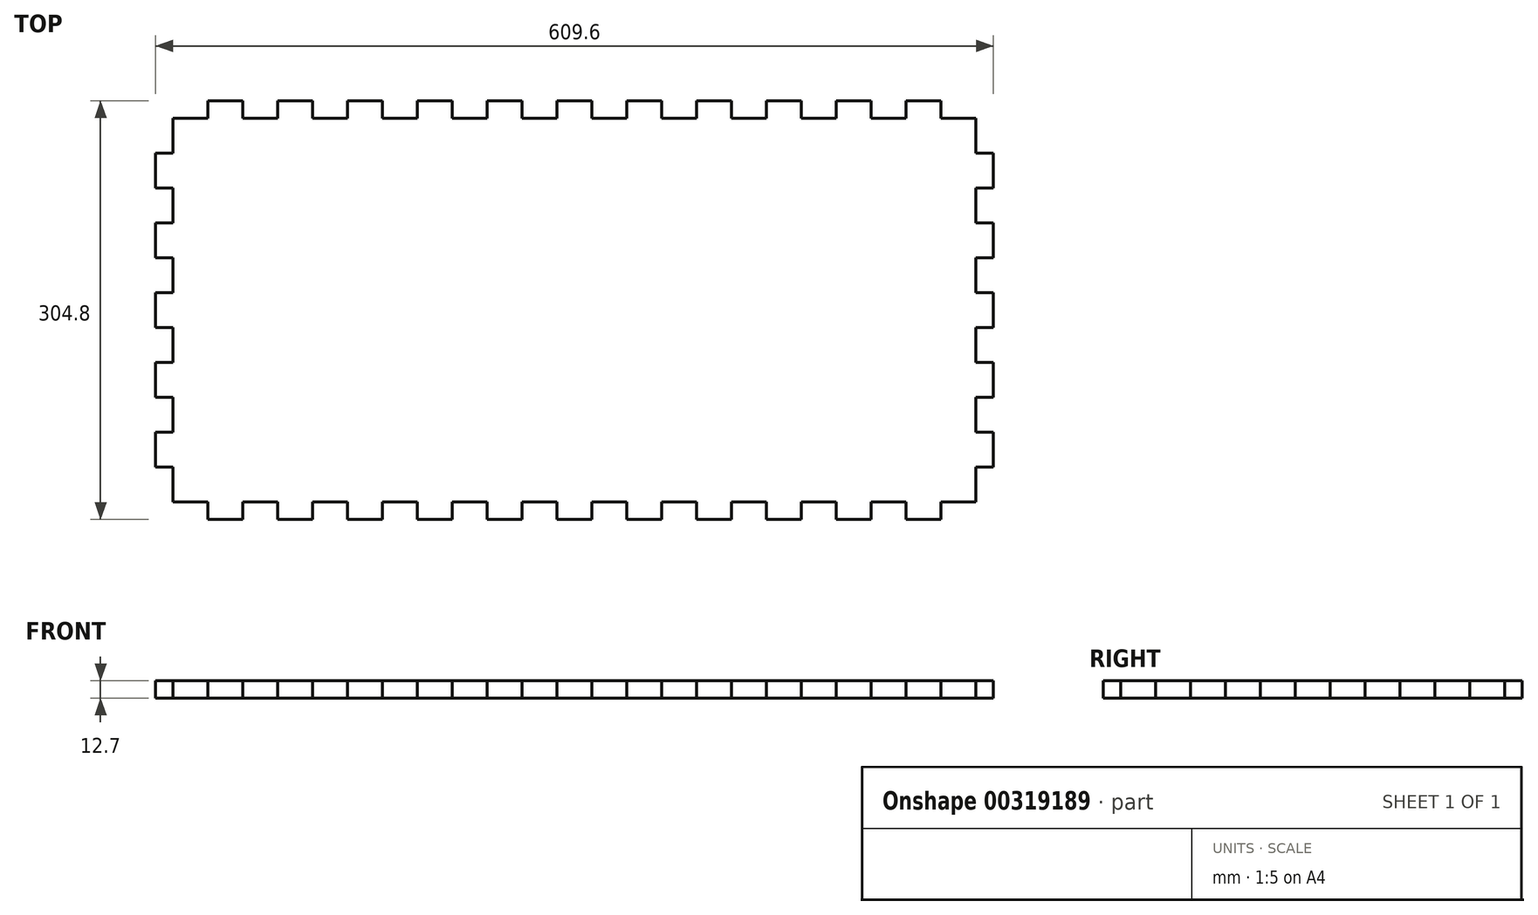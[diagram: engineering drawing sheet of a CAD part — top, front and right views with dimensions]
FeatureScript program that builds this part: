
annotation { "Feature Type Name" : "Feature", "Feature Type Description" : "" }
export const myFeature = defineFeature(function(context is Context, id is Id, definition is map)
    precondition{}
    {
        {
            var Q0;
            Q0=qCreatedBy(makeId("Top.planeOp"),FACE);
            var sketch = newSketch(context, id + "F0", { "sketchPlane" : qUnion([Q0])});
            skLineSegment(sketch, "E0.bottom", {"start": v(304.8, 152.4) * mm, "end": v(-304.8, 152.4) * mm});
            skLineSegment(sketch, "E0.top", {"start": v(304.8, -152.4) * mm, "end": v(-304.8, -152.4) * mm});
            skLineSegment(sketch, "E0.left", {"start": v(304.8, 152.4) * mm, "end": v(304.8, -152.4) * mm});
            skLineSegment(sketch, "E0.right", {"start": v(-304.8, 152.4) * mm, "end": v(-304.8, -152.4) * mm});
            skPoint(sketch, "E0.middle", {"position": v(0, 0) * mm});
            skLineSegment(sketch, "E1.bottom", {"start": v(-292.1, 152.4) * mm, "end": v(-266.7, 152.4) * mm});
            skLineSegment(sketch, "E1.top", {"start": v(-292.1, 139.7) * mm, "end": v(-266.7, 139.7) * mm});
            skLineSegment(sketch, "E1.left", {"start": v(-292.1, 152.4) * mm, "end": v(-292.1, 139.7) * mm});
            skLineSegment(sketch, "E1.right", {"start": v(-266.7, 152.4) * mm, "end": v(-266.7, 139.7) * mm});
            skLineSegment(sketch, "E2.1.0.0", {"start": v(-241.3, 152.4) * mm, "end": v(-241.3, 139.7) * mm});
            skLineSegment(sketch, "E2.1.0.1", {"start": v(-215.9, 152.4) * mm, "end": v(-215.9, 139.7) * mm});
            skLineSegment(sketch, "E2.1.0.2", {"start": v(-241.3, 139.7) * mm, "end": v(-215.9, 139.7) * mm});
            skLineSegment(sketch, "E2.1.0.3", {"start": v(-241.3, 152.4) * mm, "end": v(-215.9, 152.4) * mm});
            skLineSegment(sketch, "E2.2.0.0", {"start": v(-190.5, 152.4) * mm, "end": v(-190.5, 139.7) * mm});
            skLineSegment(sketch, "E2.2.0.1", {"start": v(-165.1, 152.4) * mm, "end": v(-165.1, 139.7) * mm});
            skLineSegment(sketch, "E2.2.0.2", {"start": v(-190.5, 139.7) * mm, "end": v(-165.1, 139.7) * mm});
            skLineSegment(sketch, "E2.2.0.3", {"start": v(-190.5, 152.4) * mm, "end": v(-165.1, 152.4) * mm});
            skLineSegment(sketch, "E2.3.0.0", {"start": v(-139.7, 152.4) * mm, "end": v(-139.7, 139.7) * mm});
            skLineSegment(sketch, "E2.3.0.1", {"start": v(-114.3, 152.4) * mm, "end": v(-114.3, 139.7) * mm});
            skLineSegment(sketch, "E2.3.0.2", {"start": v(-139.7, 139.7) * mm, "end": v(-114.3, 139.7) * mm});
            skLineSegment(sketch, "E2.3.0.3", {"start": v(-139.7, 152.4) * mm, "end": v(-114.3, 152.4) * mm});
            skLineSegment(sketch, "E2.4.0.0", {"start": v(-88.9, 152.4) * mm, "end": v(-88.9, 139.7) * mm});
            skLineSegment(sketch, "E2.4.0.1", {"start": v(-63.5, 152.4) * mm, "end": v(-63.5, 139.7) * mm});
            skLineSegment(sketch, "E2.4.0.2", {"start": v(-88.9, 139.7) * mm, "end": v(-63.5, 139.7) * mm});
            skLineSegment(sketch, "E2.4.0.3", {"start": v(-88.9, 152.4) * mm, "end": v(-63.5, 152.4) * mm});
            skLineSegment(sketch, "E2.5.0.0", {"start": v(-38.1, 152.4) * mm, "end": v(-38.1, 139.7) * mm});
            skLineSegment(sketch, "E2.5.0.1", {"start": v(-12.7, 152.4) * mm, "end": v(-12.7, 139.7) * mm});
            skLineSegment(sketch, "E2.5.0.2", {"start": v(-38.1, 139.7) * mm, "end": v(-12.7, 139.7) * mm});
            skLineSegment(sketch, "E2.5.0.3", {"start": v(-38.1, 152.4) * mm, "end": v(-12.7, 152.4) * mm});
            skLineSegment(sketch, "E2.6.0.0", {"start": v(12.7, 152.4) * mm, "end": v(12.7, 139.7) * mm});
            skLineSegment(sketch, "E2.6.0.1", {"start": v(38.1, 152.4) * mm, "end": v(38.1, 139.7) * mm});
            skLineSegment(sketch, "E2.6.0.2", {"start": v(12.7, 139.7) * mm, "end": v(38.1, 139.7) * mm});
            skLineSegment(sketch, "E2.6.0.3", {"start": v(12.7, 152.4) * mm, "end": v(38.1, 152.4) * mm});
            skLineSegment(sketch, "E2.7.0.0", {"start": v(63.5, 152.4) * mm, "end": v(63.5, 139.7) * mm});
            skLineSegment(sketch, "E2.7.0.1", {"start": v(88.9, 152.4) * mm, "end": v(88.9, 139.7) * mm});
            skLineSegment(sketch, "E2.7.0.2", {"start": v(63.5, 139.7) * mm, "end": v(88.9, 139.7) * mm});
            skLineSegment(sketch, "E2.7.0.3", {"start": v(63.5, 152.4) * mm, "end": v(88.9, 152.4) * mm});
            skLineSegment(sketch, "E2.8.0.0", {"start": v(114.3, 152.4) * mm, "end": v(114.3, 139.7) * mm});
            skLineSegment(sketch, "E2.8.0.1", {"start": v(139.7, 152.4) * mm, "end": v(139.7, 139.7) * mm});
            skLineSegment(sketch, "E2.8.0.2", {"start": v(114.3, 139.7) * mm, "end": v(139.7, 139.7) * mm});
            skLineSegment(sketch, "E2.8.0.3", {"start": v(114.3, 152.4) * mm, "end": v(139.7, 152.4) * mm});
            skLineSegment(sketch, "E2.9.0.0", {"start": v(165.1, 152.4) * mm, "end": v(165.1, 139.7) * mm});
            skLineSegment(sketch, "E2.9.0.1", {"start": v(190.5, 152.4) * mm, "end": v(190.5, 139.7) * mm});
            skLineSegment(sketch, "E2.9.0.2", {"start": v(165.1, 139.7) * mm, "end": v(190.5, 139.7) * mm});
            skLineSegment(sketch, "E2.9.0.3", {"start": v(165.1, 152.4) * mm, "end": v(190.5, 152.4) * mm});
            skLineSegment(sketch, "E2.10.0.0", {"start": v(215.9, 152.4) * mm, "end": v(215.9, 139.7) * mm});
            skLineSegment(sketch, "E2.10.0.1", {"start": v(241.3, 152.4) * mm, "end": v(241.3, 139.7) * mm});
            skLineSegment(sketch, "E2.10.0.2", {"start": v(215.9, 139.7) * mm, "end": v(241.3, 139.7) * mm});
            skLineSegment(sketch, "E2.10.0.3", {"start": v(215.9, 152.4) * mm, "end": v(241.3, 152.4) * mm});
            skLineSegment(sketch, "E2.11.0.0", {"start": v(266.7, 152.4) * mm, "end": v(266.7, 139.7) * mm});
            skLineSegment(sketch, "E2.11.0.1", {"start": v(292.1, 152.4) * mm, "end": v(292.1, 139.7) * mm});
            skLineSegment(sketch, "E2.11.0.2", {"start": v(266.7, 139.7) * mm, "end": v(292.1, 139.7) * mm});
            skLineSegment(sketch, "E2.11.0.3", {"start": v(266.7, 152.4) * mm, "end": v(292.1, 152.4) * mm});
            skLineSegment(sketch, "E2.direction1", {"start": v(-292.1, 139.7) * mm, "end": v(-241.3, 139.7) * mm, "construction": true});
            skLineSegment(sketch, "E3.bottom", {"start": v(-292.1, -152.4) * mm, "end": v(-266.7, -152.4) * mm});
            skLineSegment(sketch, "E3.top", {"start": v(-292.1, -139.7) * mm, "end": v(-266.7, -139.7) * mm});
            skLineSegment(sketch, "E3.left", {"start": v(-292.1, -152.4) * mm, "end": v(-292.1, -139.7) * mm});
            skLineSegment(sketch, "E3.right", {"start": v(-266.7, -152.4) * mm, "end": v(-266.7, -139.7) * mm});
            skLineSegment(sketch, "E4.bottom", {"start": v(-304.8, -114.3) * mm, "end": v(-292.1, -114.3) * mm});
            skLineSegment(sketch, "E4.top", {"start": v(-304.8, -139.7) * mm, "end": v(-292.1, -139.7) * mm});
            skLineSegment(sketch, "E4.left", {"start": v(-304.8, -114.3) * mm, "end": v(-304.8, -139.7) * mm});
            skLineSegment(sketch, "E4.right", {"start": v(-292.1, -114.3) * mm, "end": v(-292.1, -139.7) * mm});
            skLineSegment(sketch, "E5.1.0.0", {"start": v(-241.3, -139.7) * mm, "end": v(-215.9, -139.7) * mm});
            skLineSegment(sketch, "E5.1.0.1", {"start": v(-215.9, -152.4) * mm, "end": v(-215.9, -139.7) * mm});
            skLineSegment(sketch, "E5.1.0.2", {"start": v(-241.3, -152.4) * mm, "end": v(-241.3, -139.7) * mm});
            skLineSegment(sketch, "E5.2.0.0", {"start": v(-190.5, -139.7) * mm, "end": v(-165.1, -139.7) * mm});
            skLineSegment(sketch, "E5.2.0.1", {"start": v(-165.1, -152.4) * mm, "end": v(-165.1, -139.7) * mm});
            skLineSegment(sketch, "E5.2.0.2", {"start": v(-190.5, -152.4) * mm, "end": v(-190.5, -139.7) * mm});
            skLineSegment(sketch, "E5.3.0.0", {"start": v(-139.7, -139.7) * mm, "end": v(-114.3, -139.7) * mm});
            skLineSegment(sketch, "E5.3.0.1", {"start": v(-114.3, -152.4) * mm, "end": v(-114.3, -139.7) * mm});
            skLineSegment(sketch, "E5.3.0.2", {"start": v(-139.7, -152.4) * mm, "end": v(-139.7, -139.7) * mm});
            skLineSegment(sketch, "E5.4.0.0", {"start": v(-88.9, -139.7) * mm, "end": v(-63.5, -139.7) * mm});
            skLineSegment(sketch, "E5.4.0.1", {"start": v(-63.5, -152.4) * mm, "end": v(-63.5, -139.7) * mm});
            skLineSegment(sketch, "E5.4.0.2", {"start": v(-88.9, -152.4) * mm, "end": v(-88.9, -139.7) * mm});
            skLineSegment(sketch, "E5.5.0.0", {"start": v(-38.1, -139.7) * mm, "end": v(-12.7, -139.7) * mm});
            skLineSegment(sketch, "E5.5.0.1", {"start": v(-12.7, -152.4) * mm, "end": v(-12.7, -139.7) * mm});
            skLineSegment(sketch, "E5.5.0.2", {"start": v(-38.1, -152.4) * mm, "end": v(-38.1, -139.7) * mm});
            skLineSegment(sketch, "E5.6.0.0", {"start": v(12.7, -139.7) * mm, "end": v(38.1, -139.7) * mm});
            skLineSegment(sketch, "E5.6.0.1", {"start": v(38.1, -152.4) * mm, "end": v(38.1, -139.7) * mm});
            skLineSegment(sketch, "E5.6.0.2", {"start": v(12.7, -152.4) * mm, "end": v(12.7, -139.7) * mm});
            skLineSegment(sketch, "E5.7.0.0", {"start": v(63.5, -139.7) * mm, "end": v(88.9, -139.7) * mm});
            skLineSegment(sketch, "E5.7.0.1", {"start": v(88.9, -152.4) * mm, "end": v(88.9, -139.7) * mm});
            skLineSegment(sketch, "E5.7.0.2", {"start": v(63.5, -152.4) * mm, "end": v(63.5, -139.7) * mm});
            skLineSegment(sketch, "E5.8.0.0", {"start": v(114.3, -139.7) * mm, "end": v(139.7, -139.7) * mm});
            skLineSegment(sketch, "E5.8.0.1", {"start": v(139.7, -152.4) * mm, "end": v(139.7, -139.7) * mm});
            skLineSegment(sketch, "E5.8.0.2", {"start": v(114.3, -152.4) * mm, "end": v(114.3, -139.7) * mm});
            skLineSegment(sketch, "E5.9.0.0", {"start": v(165.1, -139.7) * mm, "end": v(190.5, -139.7) * mm});
            skLineSegment(sketch, "E5.9.0.1", {"start": v(190.5, -152.4) * mm, "end": v(190.5, -139.7) * mm});
            skLineSegment(sketch, "E5.9.0.2", {"start": v(165.1, -152.4) * mm, "end": v(165.1, -139.7) * mm});
            skLineSegment(sketch, "E5.10.0.0", {"start": v(215.9, -139.7) * mm, "end": v(241.3, -139.7) * mm});
            skLineSegment(sketch, "E5.10.0.1", {"start": v(241.3, -152.4) * mm, "end": v(241.3, -139.7) * mm});
            skLineSegment(sketch, "E5.10.0.2", {"start": v(215.9, -152.4) * mm, "end": v(215.9, -139.7) * mm});
            skLineSegment(sketch, "E5.11.0.0", {"start": v(266.7, -139.7) * mm, "end": v(292.1, -139.7) * mm});
            skLineSegment(sketch, "E5.11.0.1", {"start": v(292.1, -152.4) * mm, "end": v(292.1, -139.7) * mm});
            skLineSegment(sketch, "E5.11.0.2", {"start": v(266.7, -152.4) * mm, "end": v(266.7, -139.7) * mm});
            skLineSegment(sketch, "E5.direction1", {"start": v(-292.1, -139.7) * mm, "end": v(-241.3, -139.7) * mm, "construction": true});
            skLineSegment(sketch, "E6.0.1.0", {"start": v(-304.8, -88.9) * mm, "end": v(-292.1, -88.9) * mm});
            skLineSegment(sketch, "E6.0.1.1", {"start": v(-292.1, -63.5) * mm, "end": v(-292.1, -88.9) * mm});
            skLineSegment(sketch, "E6.0.1.2", {"start": v(-304.8, -63.5) * mm, "end": v(-292.1, -63.5) * mm});
            skLineSegment(sketch, "E6.0.2.0", {"start": v(-304.8, -38.1) * mm, "end": v(-292.1, -38.1) * mm});
            skLineSegment(sketch, "E6.0.2.1", {"start": v(-292.1, -12.7) * mm, "end": v(-292.1, -38.1) * mm});
            skLineSegment(sketch, "E6.0.2.2", {"start": v(-304.8, -12.7) * mm, "end": v(-292.1, -12.7) * mm});
            skLineSegment(sketch, "E6.0.3.0", {"start": v(-304.8, 12.7) * mm, "end": v(-292.1, 12.7) * mm});
            skLineSegment(sketch, "E6.0.3.1", {"start": v(-292.1, 38.1) * mm, "end": v(-292.1, 12.7) * mm});
            skLineSegment(sketch, "E6.0.3.2", {"start": v(-304.8, 38.1) * mm, "end": v(-292.1, 38.1) * mm});
            skLineSegment(sketch, "E6.0.4.0", {"start": v(-304.8, 63.5) * mm, "end": v(-292.1, 63.5) * mm});
            skLineSegment(sketch, "E6.0.4.1", {"start": v(-292.1, 88.9) * mm, "end": v(-292.1, 63.5) * mm});
            skLineSegment(sketch, "E6.0.4.2", {"start": v(-304.8, 88.9) * mm, "end": v(-292.1, 88.9) * mm});
            skLineSegment(sketch, "E6.0.5.0", {"start": v(-304.8, 114.3) * mm, "end": v(-292.1, 114.3) * mm});
            skLineSegment(sketch, "E6.0.5.1", {"start": v(-292.1, 139.7) * mm, "end": v(-292.1, 114.3) * mm});
            skLineSegment(sketch, "E6.0.5.2", {"start": v(-304.8, 139.7) * mm, "end": v(-292.1, 139.7) * mm});
            skLineSegment(sketch, "E6.direction1", {"start": v(-304.8, -139.7) * mm, "end": v(-279.4, -139.7) * mm, "construction": true});
            skLineSegment(sketch, "E6.direction2", {"start": v(-304.8, -139.7) * mm, "end": v(-304.8, -88.9) * mm, "construction": true});
            skLineSegment(sketch, "E7.bottom", {"start": v(304.8, -139.7) * mm, "end": v(292.1, -139.7) * mm});
            skLineSegment(sketch, "E7.top", {"start": v(304.8, -114.3) * mm, "end": v(292.1, -114.3) * mm});
            skLineSegment(sketch, "E7.left", {"start": v(304.8, -139.7) * mm, "end": v(304.8, -114.3) * mm});
            skLineSegment(sketch, "E7.right", {"start": v(292.1, -139.7) * mm, "end": v(292.1, -114.3) * mm});
            skLineSegment(sketch, "E8.0.1.0", {"start": v(304.8, -88.9) * mm, "end": v(304.8, -63.5) * mm});
            skLineSegment(sketch, "E8.0.1.1", {"start": v(304.8, -63.5) * mm, "end": v(292.1, -63.5) * mm});
            skLineSegment(sketch, "E8.0.1.2", {"start": v(304.8, -88.9) * mm, "end": v(292.1, -88.9) * mm});
            skLineSegment(sketch, "E8.0.1.3", {"start": v(292.1, -88.9) * mm, "end": v(292.1, -63.5) * mm});
            skLineSegment(sketch, "E8.0.2.0", {"start": v(304.8, -38.1) * mm, "end": v(304.8, -12.7) * mm});
            skLineSegment(sketch, "E8.0.2.1", {"start": v(304.8, -12.7) * mm, "end": v(292.1, -12.7) * mm});
            skLineSegment(sketch, "E8.0.2.2", {"start": v(304.8, -38.1) * mm, "end": v(292.1, -38.1) * mm});
            skLineSegment(sketch, "E8.0.2.3", {"start": v(292.1, -38.1) * mm, "end": v(292.1, -12.7) * mm});
            skLineSegment(sketch, "E8.0.3.0", {"start": v(304.8, 12.7) * mm, "end": v(304.8, 38.1) * mm});
            skLineSegment(sketch, "E8.0.3.1", {"start": v(304.8, 38.1) * mm, "end": v(292.1, 38.1) * mm});
            skLineSegment(sketch, "E8.0.3.2", {"start": v(304.8, 12.7) * mm, "end": v(292.1, 12.7) * mm});
            skLineSegment(sketch, "E8.0.3.3", {"start": v(292.1, 12.7) * mm, "end": v(292.1, 38.1) * mm});
            skLineSegment(sketch, "E8.0.4.0", {"start": v(304.8, 63.5) * mm, "end": v(304.8, 88.9) * mm});
            skLineSegment(sketch, "E8.0.4.1", {"start": v(304.8, 88.9) * mm, "end": v(292.1, 88.9) * mm});
            skLineSegment(sketch, "E8.0.4.2", {"start": v(304.8, 63.5) * mm, "end": v(292.1, 63.5) * mm});
            skLineSegment(sketch, "E8.0.4.3", {"start": v(292.1, 63.5) * mm, "end": v(292.1, 88.9) * mm});
            skLineSegment(sketch, "E8.0.5.0", {"start": v(304.8, 114.3) * mm, "end": v(304.8, 139.7) * mm});
            skLineSegment(sketch, "E8.0.5.1", {"start": v(304.8, 139.7) * mm, "end": v(292.1, 139.7) * mm});
            skLineSegment(sketch, "E8.0.5.2", {"start": v(304.8, 114.3) * mm, "end": v(292.1, 114.3) * mm});
            skLineSegment(sketch, "E8.0.5.3", {"start": v(292.1, 114.3) * mm, "end": v(292.1, 139.7) * mm});
            skLineSegment(sketch, "E8.direction1", {"start": v(292.1, -139.7) * mm, "end": v(317.5, -139.7) * mm, "construction": true});
            skLineSegment(sketch, "E8.direction2", {"start": v(292.1, -139.7) * mm, "end": v(292.1, -88.9) * mm, "construction": true});
            skSolve(sketch);
        }
        {
            var Q0;
            Q0=makeQuery(id+"F0.imprint","IMPRINT",FACE,{"disambiguationData":[TD([[makeQuery(id+"F0.imprint","IMPRINT",EDGE,{"derivedFrom":sQuery(id+"F0.wireOp",EDGE,"E1.top")}),-1.0]])]});
            extrude(context, id + "F1", {"entities" : qUnion([Q0]), "depth" : 12.7 * mm});
        }
    });
